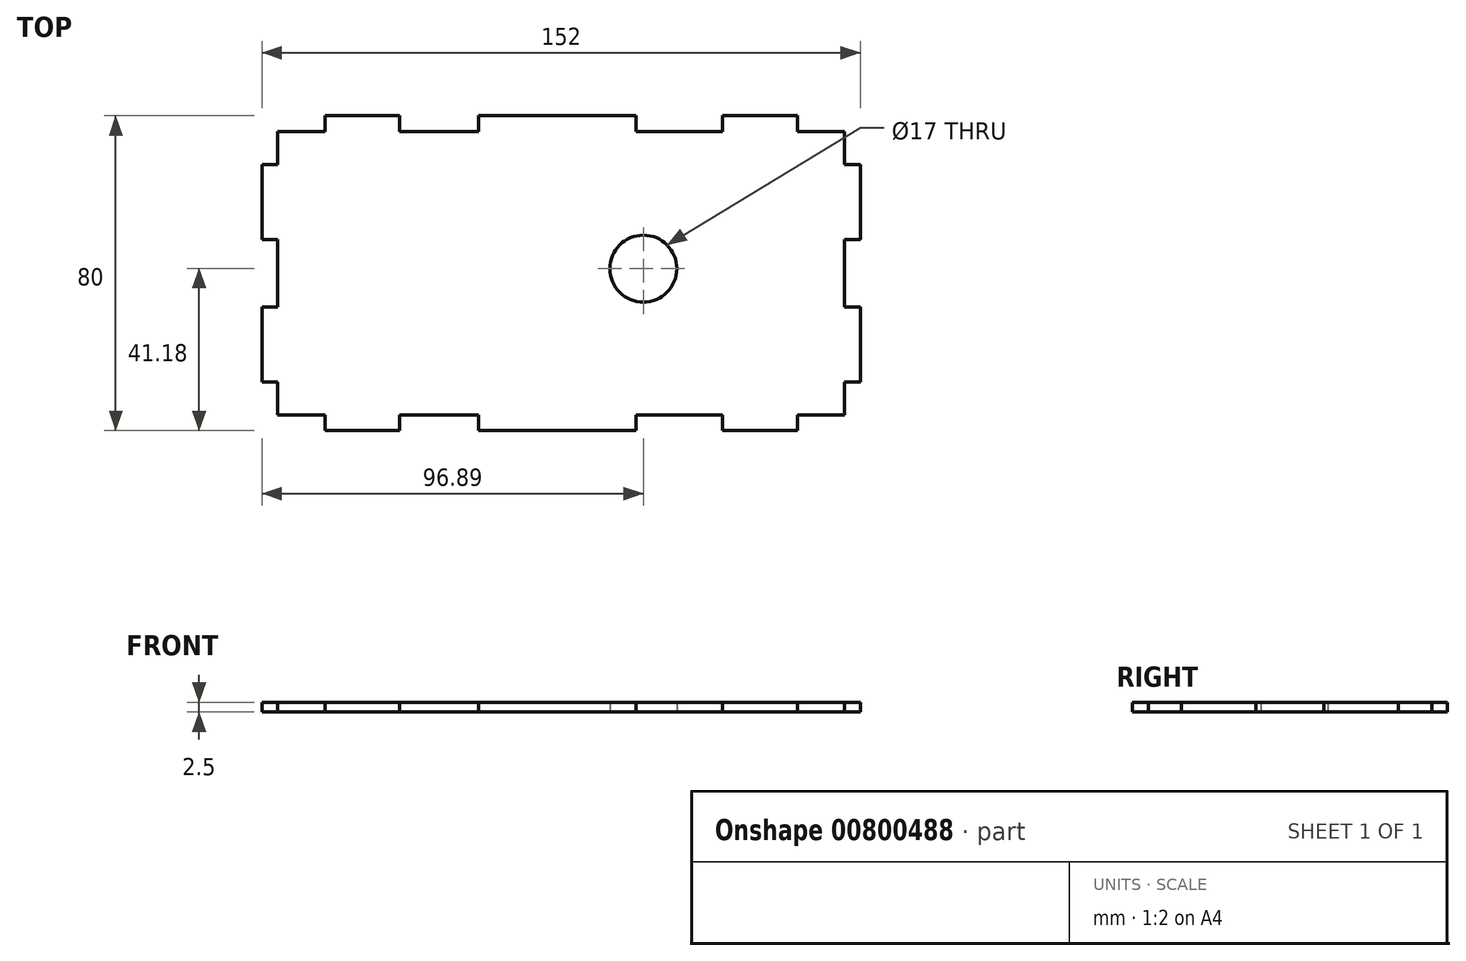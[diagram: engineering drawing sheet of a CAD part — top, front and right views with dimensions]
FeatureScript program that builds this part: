
annotation { "Feature Type Name" : "Feature", "Feature Type Description" : "" }
export const myFeature = defineFeature(function(context is Context, id is Id, definition is map)
    precondition{}
    {
        {
            var Q0;
            Q0=qCreatedBy(makeId("Top.planeOp"),FACE);
            var sketch = newSketch(context, id + "F0", { "sketchPlane" : qUnion([Q0])});
            skLineSegment(sketch, "E0.bottom", {"start": v(-72, 36) * mm, "end": v(72, 36) * mm});
            skLineSegment(sketch, "E0.top", {"start": v(-72, -36) * mm, "end": v(72, -36) * mm});
            skLineSegment(sketch, "E0.left", {"start": v(-72, 36) * mm, "end": v(-72, -36) * mm});
            skLineSegment(sketch, "E0.right", {"start": v(72, 36) * mm, "end": v(72, -36) * mm});
            skPoint(sketch, "E0.middle", {"position": v(0, 0) * mm});
            skLineSegment(sketch, "E1", {"start": v(-72, 36) * mm, "end": v(-60, 36) * mm});
            skLineSegment(sketch, "E2", {"start": v(-60, 36) * mm, "end": v(-60, 40) * mm});
            skLineSegment(sketch, "E3", {"start": v(-60, 40) * mm, "end": v(-41, 40) * mm});
            skLineSegment(sketch, "E4", {"start": v(-41, 40) * mm, "end": v(-41, 36) * mm});
            skLineSegment(sketch, "E5", {"start": v(-41, 36) * mm, "end": v(-21, 36) * mm});
            skLineSegment(sketch, "E6", {"start": v(-21, 36) * mm, "end": v(-21, 40) * mm});
            skLineSegment(sketch, "E7", {"start": v(-21, 40) * mm, "end": v(19, 40) * mm});
            skLineSegment(sketch, "E8", {"start": v(19, 40) * mm, "end": v(19, 36) * mm});
            skLineSegment(sketch, "E9", {"start": v(19, 36) * mm, "end": v(41, 36) * mm});
            skLineSegment(sketch, "E10.MirrorCS", {"start": v(-60, -36) * mm, "end": v(-60, -40) * mm});
            skLineSegment(sketch, "E11.MirrorCS", {"start": v(-60, -40) * mm, "end": v(-41, -40) * mm});
            skLineSegment(sketch, "E12.MirrorCS", {"start": v(-41, -40) * mm, "end": v(-41, -36) * mm});
            skLineSegment(sketch, "E13.MirrorCS", {"start": v(-21, -36) * mm, "end": v(-21, -40) * mm});
            skLineSegment(sketch, "E14.MirrorCS", {"start": v(-21, -40) * mm, "end": v(19, -40) * mm});
            skLineSegment(sketch, "E15.MirrorCS", {"start": v(19, -40) * mm, "end": v(19, -36) * mm});
            skLineSegment(sketch, "E16.MirrorCS", {"start": v(41, -36) * mm, "end": v(41, -40) * mm});
            skLineSegment(sketch, "E17.MirrorCS", {"start": v(41, -40) * mm, "end": v(60, -40) * mm});
            skLineSegment(sketch, "E18.MirrorCS", {"start": v(60, -40) * mm, "end": v(60, -36) * mm});
            skLineSegment(sketch, "E19", {"start": v(-72, -36) * mm, "end": v(-72, -27.6) * mm});
            skLineSegment(sketch, "E20", {"start": v(-72, -27.6) * mm, "end": v(-76, -27.6) * mm});
            skLineSegment(sketch, "E21", {"start": v(-76, -27.6) * mm, "end": v(-76, -8.6) * mm});
            skLineSegment(sketch, "E22", {"start": v(-76, -8.6) * mm, "end": v(-72, -8.6) * mm});
            skLineSegment(sketch, "E23.MirrorCS", {"start": v(-76, 8.6) * mm, "end": v(-72, 8.6) * mm});
            skLineSegment(sketch, "E24.MirrorCS", {"start": v(-76, 27.6) * mm, "end": v(-76, 8.6) * mm});
            skLineSegment(sketch, "E25.MirrorCS", {"start": v(-72, 27.6) * mm, "end": v(-76, 27.6) * mm});
            skLineSegment(sketch, "E26.MirrorCS", {"start": v(72, 27.6) * mm, "end": v(76, 27.6) * mm});
            skLineSegment(sketch, "E27.MirrorCS", {"start": v(76, 27.6) * mm, "end": v(76, 8.6) * mm});
            skLineSegment(sketch, "E28.MirrorCS", {"start": v(76, 8.6) * mm, "end": v(72, 8.6) * mm});
            skLineSegment(sketch, "E29.MirrorCS", {"start": v(76, -8.6) * mm, "end": v(72, -8.6) * mm});
            skLineSegment(sketch, "E30.MirrorCS", {"start": v(76, -27.6) * mm, "end": v(76, -8.6) * mm});
            skLineSegment(sketch, "E31.MirrorCS", {"start": v(72, -27.6) * mm, "end": v(76, -27.6) * mm});
            skLineSegment(sketch, "E32.MirrorCS", {"start": v(60, 40) * mm, "end": v(41, 40) * mm});
            skLineSegment(sketch, "E33.MirrorCS", {"start": v(60, 36) * mm, "end": v(60, 40) * mm});
            skLineSegment(sketch, "E34.MirrorCS", {"start": v(41, 40) * mm, "end": v(41, 36) * mm});
            skCircle(sketch, "E35", {"center": v(20.9, 1.18) * mm, "radius": 8.5 * mm});
            skSolve(sketch);
        }
        {
            var Q0;
            {var subQ0=sQuery(id+"F0.wireOp",EDGE,"E2");Q0=makeQuery(id+"F0.imprint","IMPRINT",FACE,{"disambiguationData":[TD([[makeQuery(id+"F0.imprint","IMPRINT",EDGE,{"derivedFrom":subQ0}),-1.0]])]});}
            var Q1;
            {var subQ0=sQuery(id+"F0.wireOp",EDGE,"E6");Q1=makeQuery(id+"F0.imprint","IMPRINT",FACE,{"disambiguationData":[TD([[makeQuery(id+"F0.imprint","IMPRINT",EDGE,{"derivedFrom":subQ0}),-1.0]])]});}
            var Q2;
            Q2=makeQuery(id+"F0.imprint","IMPRINT",FACE,{"disambiguationData":[TD([[makeQuery(id+"F0.imprint","IMPRINT",EDGE,{"derivedFrom":sQuery(id+"F0.wireOp",EDGE,"E32.MirrorCS")}),1.0]])]});
            var Q3;
            {var subQ0=sQuery(id+"F0.wireOp",EDGE,"E10.MirrorCS");Q3=makeQuery(id+"F0.imprint","IMPRINT",FACE,{"disambiguationData":[TD([[makeQuery(id+"F0.imprint","IMPRINT",EDGE,{"derivedFrom":subQ0}),1.0]])]});}
            var Q4;
            {var subQ0=sQuery(id+"F0.wireOp",EDGE,"E13.MirrorCS");Q4=makeQuery(id+"F0.imprint","IMPRINT",FACE,{"disambiguationData":[TD([[makeQuery(id+"F0.imprint","IMPRINT",EDGE,{"derivedFrom":subQ0}),1.0]])]});}
            var Q5;
            {var subQ0=sQuery(id+"F0.wireOp",EDGE,"E16.MirrorCS");Q5=makeQuery(id+"F0.imprint","IMPRINT",FACE,{"disambiguationData":[TD([[makeQuery(id+"F0.imprint","IMPRINT",EDGE,{"derivedFrom":subQ0}),1.0]])]});}
            var Q6;
            {var subQ2=sQuery(id+"F0.wireOp",EDGE,"E23.MirrorCS");Q6=makeQuery(id+"F0.imprint","IMPRINT",FACE,{"disambiguationData":[TD([[makeQuery(id+"F0.imprint","IMPRINT",EDGE,{"derivedFrom":subQ2}),1.0]])]});}
            var Q7;
            {var subQ0=sQuery(id+"F0.wireOp",EDGE,"E20");Q7=makeQuery(id+"F0.imprint","IMPRINT",FACE,{"disambiguationData":[TD([[makeQuery(id+"F0.imprint","IMPRINT",EDGE,{"derivedFrom":subQ0}),-1.0]])]});}
            var Q8;
            {var subQ0=sQuery(id+"F0.wireOp",EDGE,"E26.MirrorCS");Q8=makeQuery(id+"F0.imprint","IMPRINT",FACE,{"disambiguationData":[TD([[makeQuery(id+"F0.imprint","IMPRINT",EDGE,{"derivedFrom":subQ0}),-1.0]])]});}
            var Q9;
            {var subQ0=sQuery(id+"F0.wireOp",EDGE,"E29.MirrorCS");Q9=makeQuery(id+"F0.imprint","IMPRINT",FACE,{"disambiguationData":[TD([[makeQuery(id+"F0.imprint","IMPRINT",EDGE,{"derivedFrom":subQ0}),1.0]])]});}
            var Q10;
            Q10=makeQuery(id+"F0.imprint","IMPRINT",FACE,{"disambiguationData":[TD([[makeQuery(id+"F0.imprint","IMPRINT",EDGE,{"derivedFrom":sQuery(id+"F0.wireOp",EDGE,"E35")}),-1.0]])]});
            extrude(context, id + "F1", {"entities" : qUnion([Q0, Q1, Q2, Q3, Q4, Q5, Q6, Q7, Q8, Q9, Q10]), "depth" : 2.5 * mm, "offsetDistance" : 25 * mm});
        }
    });
